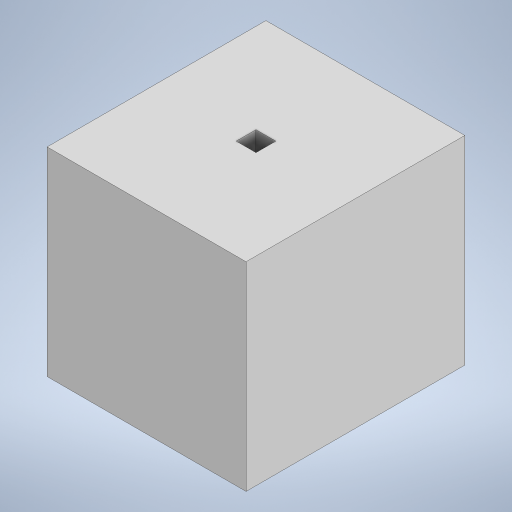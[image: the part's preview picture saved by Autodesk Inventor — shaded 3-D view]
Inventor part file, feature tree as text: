
AUTODESK INVENTOR PART (.ipt)
format: ipt  version: 2023 (Build 270158000, 158)  size: 272,384 bytes
history: native  units: in
note: dims shown in document units (in); Inventor stores cm internally (conversion verified against a paired STEP export)
features: sketch x2, extrude x2
ambient origin geometry x8: Origin, YZ Plane, XZ Plane, XY Plane, X Axis, Y Axis, Z Axis, Center Point
bodies: Solid1 (feature_tree)
feature tree (4):
  sketch  "Sketch4"  dims[d8=7.874in d9=3.937in]
  sketch  "Sketch5"  dims[d10=3.5433in d11=0.7874in d12=7.874in d13=3.937in d14=7.874in d15=3.937in d16=3.5433in d17=0.7874in d18=3.5433in d19=0.7874in d20=7.874in d21=0.0in d22=7.874in d23=0.0in]
  extrude  "Extrusion1"  Depth=3.937in
  extrude  "Extrusion2"  Depth=0.7874in
